# Revit family: Betonafstandsklods med wire 20-25-30
name_source: partatom
category: Generic Models
units: mm (PartAtom-declared; Revit-internal decimal feet)

## family parameters
Always vertical = No
Can host rebar = No
Cut with Voids When Loaded = No
Part Type = Normal
Room Calculation Point = No
Round Connector Dimension = Use Diameter
Shared = No
Work Plane-Based = Yes

## types (1)
- Betonafstandsklods med wire 20-25-30
    Bottom Curve = 18 mm  [stored 0.0590551 ft]
    Default Elevation = 1219 mm
    Height = 27 mm  [stored 0.0885827 ft]
    Metal = Metal
    Numbers = Wall Texture, Orange Peel
    Side Curve = 18 mm  [stored 0.0590551 ft]
    Side Curve R = 20 mm  [stored 0.0656168 ft]
    Technical Data Sheet = https://haucon.dk
    Thickness = 22 mm  [stored 0.0721785 ft]
    Top Curve = 8 mm  [stored 0.0262467 ft]
    Top Curve R = 15 mm  [stored 0.0492126 ft]
    Website Link = https://haucon.dk
    Width = 32 mm  [stored 0.104987 ft]
    concrete = Concrete, C50/60

note: [stored X ft] marks values corroborated as IEEE doubles in the binary element streams (Revit-internal decimal feet)

## geometry (parser evidence)
native form markers: Sweep x2
no freeform markers — native parametric forms only
